# Revit family: Doors_Swing_Avanti_Systems_Timber-Swing-Doors-Dbl-Glazed
name_source: partatom
category: Doors
revit_build: Autodesk Revit Architecture 2015 (Build: 20140606_1530(x64)
units: mm (PartAtom-declared; Revit-internal decimal feet)

## types (1)
- Timber Door 1 7/8"
    Acoustic performance (dB) = 36
    Analytic Construction = <None>
    BIMobject category = Swing
    BIMobject category code = doors-swing
    BIMobject main category = Doors
    BIMobject main category code = doors
    Brand url = http://www.avantisystemsusa.com
    Description = Ideally suited for Conference Rooms, Offices or other spaces where a good sound insulation and reliability is required.
    Design country = United States
    Edition number = 1
    Function = Interior
    Handle Distance = 4"
    IFC Classification = Door
    LEED compatibility = YES
    Manufacturer = Avanti Systems USA
    Manufacturer name = Avanti Systems
    Masterformat 2014 Code = 08 14 00
    Masterformat 2014 Description = Wood Doors
    Material main = Wood
    Material secondary = Aluminium
    Model = Timber Swing Doors
    Nominal height = 0"
    Nominal width = 0"
    OmniClass Code = 23-17 11 15
    OmniClass Description = Wood Doors
    Product Guid = ecfd7a65-91a6-4286-8425-fb7562b3b134
    Product SKU = avanti-timber
    Product data url = https://bimobject.com
    Product family = Pivot & Hinged Doors
    Product group = Timber
    Product url = https://www.avantisystemsusa.com
    QR code = http://bimobject.com
    Sound Rating = 0
    Thickness = 2"
    UNSPSC Code = 30171504
    URL = https://www.avantisystemsusa.com
    Uniclass 1.4 Code = JL20
    Uniclass 1.4 Description = Doors
    Uniclass 2015 Code = EF_25_30
    Uniclass 2015 Name = Doors and windows
    Uniformat II Code = C1020
    Uniformat II Description = Interior Doors
    Warranty = 1 year
    Weight Net (Kg) = 0

## geometry (parser evidence)
native form markers: Sweep x17
no freeform markers — native parametric forms only
